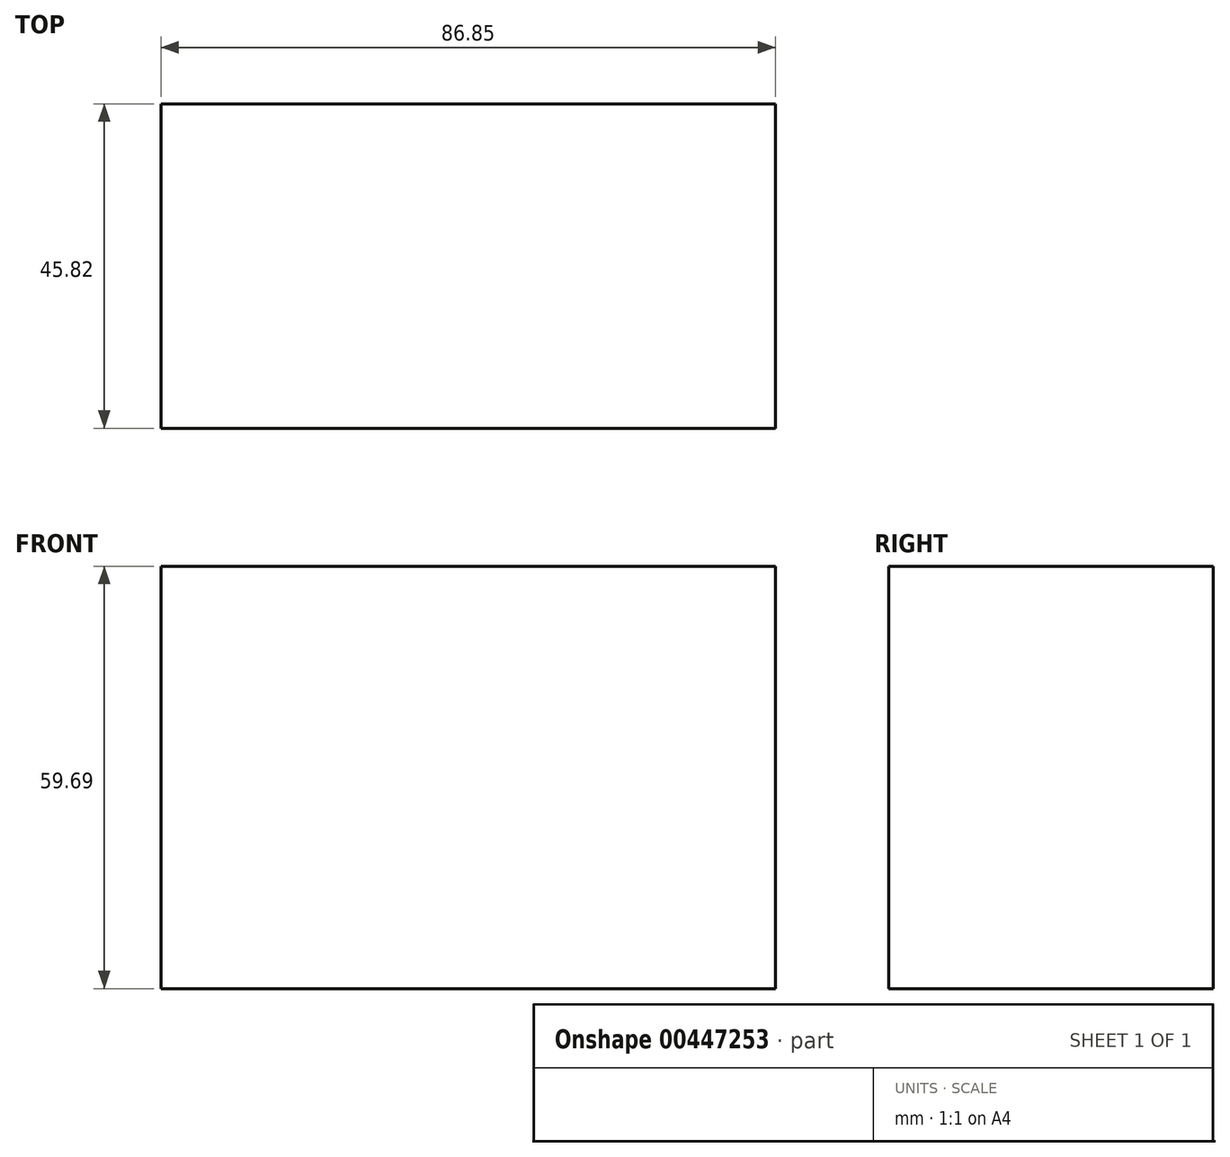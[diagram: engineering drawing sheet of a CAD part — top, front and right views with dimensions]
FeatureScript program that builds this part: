
annotation { "Feature Type Name" : "Feature", "Feature Type Description" : "" }
export const myFeature = defineFeature(function(context is Context, id is Id, definition is map)
    precondition{}
    {
        {
            var Q0;
            Q0=qCreatedBy(makeId("Top.planeOp"),FACE);
            var sketch = newSketch(context, id + "F0", { "sketchPlane" : qUnion([Q0])});
            skLineSegment(sketch, "E0.bottom", {"start": v(-24.43, 46.06) * mm, "end": v(62.42, 46.06) * mm});
            skLineSegment(sketch, "E0.top", {"start": v(-24.43, 0.24) * mm, "end": v(62.42, 0.24) * mm});
            skLineSegment(sketch, "E0.left", {"start": v(62.42, 46.06) * mm, "end": v(62.42, 0.24) * mm});
            skLineSegment(sketch, "E0.right", {"start": v(-24.43, 46.06) * mm, "end": v(-24.43, 0.24) * mm});
            skSolve(sketch);
        }
        {
            var Q0;
            Q0=makeQuery(id+"F0.imprint","IMPRINT",FACE,{"disambiguationData":[TD([[makeQuery(id+"F0.imprint","IMPRINT",EDGE,{"derivedFrom":sQuery(id+"F0.wireOp",EDGE,"E0.bottom")}),-1.0]])]});
            extrude(context, id + "F1", {"entities" : qUnion([Q0]), "depth" : 59.69 * mm});
        }
    });
